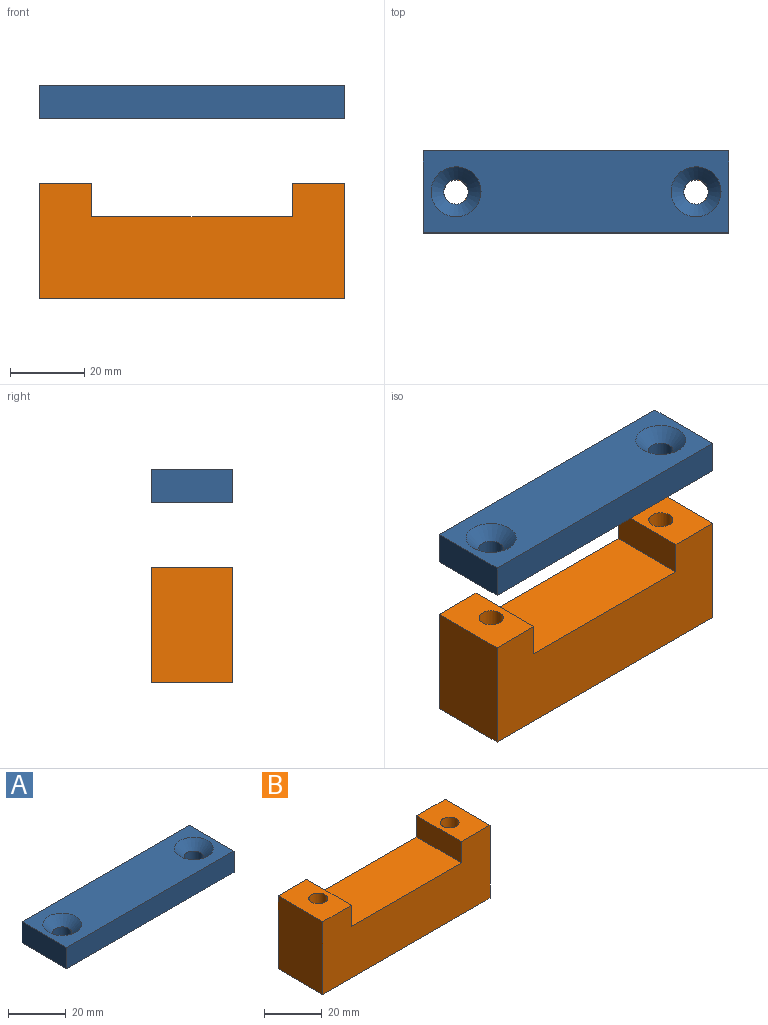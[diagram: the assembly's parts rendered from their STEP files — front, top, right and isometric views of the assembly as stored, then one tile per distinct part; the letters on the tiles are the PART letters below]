
ASSEMBLY  parts=2 mates=2
PART A: 10 faces, bbox 82x22x9 mm
  f0: plane 22x9mm, normal (-1,0,0), area 198mm2, adj f1,f3,f4,f5
  f1: plane 82x9mm, normal (0,-1,0), area 738mm2, adj f0,f2,f4,f5
  f2: plane 22x9mm, normal (1,0,0), area 198mm2, adj f1,f3,f4,f5
  f3: plane 82x9mm, normal (0,1,0), area 738mm2, adj f0,f2,f4,f5
  f4: plane 82x22mm, normal (0,0,1), area 1520.3mm2, adj f0,f1,f2,f3,f7,f9
  f5: plane 82x22mm, normal (0,0,-1), area 1735.6mm2, adj f0,f1,f2,f3,f6,f8
  f6: cylinder r=3.3mm len=6.6mm, axis (0,0,1), area 115.7mm2, adj f5,f7
  f7: cone r=3.3mm half-angle=45deg, axis (0,0,1), area 152.3mm2, adj f4,f6
  f8: cylinder r=3.3mm len=6.6mm, axis (0,0,1), area 115.7mm2, adj f5,f9
  f9: cone r=3.3mm half-angle=45deg, axis (0,0,1), area 152.3mm2, adj f4,f8
PART B: 12 faces, bbox 82x22x31 mm
  f0: plane 31x22mm, normal (-1,0,0), area 682mm2, adj f1,f7,f8,f9
  f1: plane 82x22mm, normal (0,0,-1), area 1737.6mm2, adj f0,f2,f8,f9,f10,f11
  f2: plane 31x22mm, normal (1,0,0), area 682mm2, adj f1,f3,f8,f9
  f3: plane 22x14mm, normal (0,0,1), area 274.8mm2, adj f2,f4,f8,f9,f11
  f4: plane 22x9mm, normal (-1,0,0), area 198mm2, adj f3,f5,f8,f9
  f5: plane 54x22mm, normal (0,0,1), area 1188mm2, adj f4,f6,f8,f9
  f6: plane 22x9mm, normal (1,0,0), area 198mm2, adj f5,f7,f8,f9
  f7: plane 22x14mm, normal (0,0,1), area 274.8mm2, adj f0,f6,f8,f9,f10
  f8: plane 82x31mm, normal (0,-1,0), area 2056mm2, adj f0,f1,f2,f3,f4,f5,f6,f7
  f9: plane 82x31mm, normal (0,1,0), area 2056mm2, adj f0,f1,f2,f3,f4,f5,f6,f7
  f10: cylinder r=3.25mm len=31mm, axis (0,0,1), area 633mm2, adj f1,f7
  f11: cylinder r=3.25mm len=31mm, axis (0,0,1), area 633mm2, adj f1,f3
PLACE A t=(-10.85,6.01,-11.96)mm
PLACE B t=(-10.85,28.01,-60.24)mm
MATE planar A.f2 <-> B.f2  axis (1,0,0) through (71.15,17.01,-7.46)mm
MATE planar A.f1 <-> B.f8  axis (0,-1,0) through (30.15,6.01,-7.46)mm
